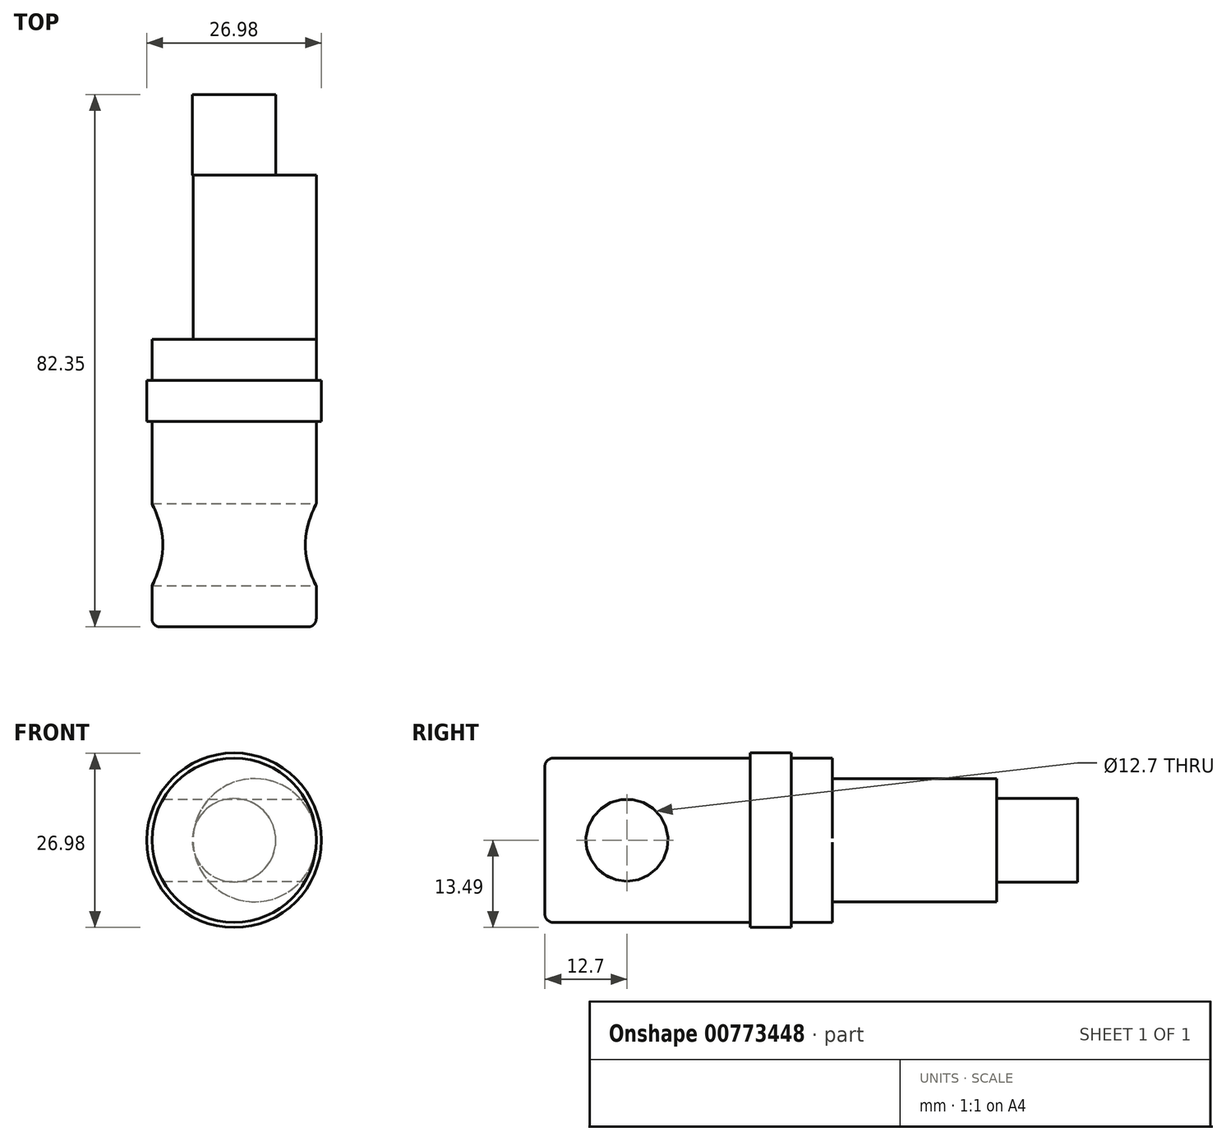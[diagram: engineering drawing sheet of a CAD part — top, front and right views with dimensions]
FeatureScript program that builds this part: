
annotation { "Feature Type Name" : "Feature", "Feature Type Description" : "" }
export const myFeature = defineFeature(function(context is Context, id is Id, definition is map)
    precondition{}
    {
        {
            var Q0;
            Q0=qCreatedBy(makeId("Front.planeOp"),FACE);
            var sketch = newSketch(context, id + "F0", { "sketchPlane" : qUnion([Q0])});
            skCircle(sketch, "E0", {"center": v(0, 0) * mm, "radius": 6.45 * mm});
            skSolve(sketch);
        }
        {
            var Q0;
            Q0 = qSketchRegion(id + "F0", true);
            extrude(context, id + "F1", {"entities" : qUnion([Q0]), "depth" : 12.5 * mm, "offsetDistance" : 25.4 * mm});
        }
        {
            var Q0;
            Q0=makeQuery(id+"F1.opExtrude","CAP_FACE",FACE,{"disambiguationData":[OSD([sQuery(id+"F0.wireOp",EDGE,"E0")])],"isStart":false});
            var sketch = newSketch(context, id + "F2", { "sketchPlane" : qUnion([Q0])});
            skPoint(sketch, "E1", {"position": v(3.18, 0) * mm});
            skCircle(sketch, "E2", {"center": v(3.18, 0) * mm, "radius": 9.52 * mm});
            skSolve(sketch);
        }
        {
            var Q0;
            Q0 = qSketchRegion(id + "F2", true);
            extrude(context, id + "F3", {"entities" : qUnion([Q0]), "operationType" : NewBodyOperationType.ADD, "depth" : 25.4 * mm, "offsetDistance" : 25.4 * mm});
        }
        {
            var Q0;
            Q0=makeQuery(id+"F3.opExtrude","CAP_FACE",FACE,{"disambiguationData":[OSD([sQuery(id+"F2.wireOp",EDGE,"E2")])],"isStart":false});
            var sketch = newSketch(context, id + "F4", { "sketchPlane" : qUnion([Q0])});
            skCircle(sketch, "E3", {"center": v(0, 0) * mm, "radius": 12.7 * mm});
            skSolve(sketch);
        }
        {
            var Q0;
            Q0 = qSketchRegion(id + "F4", true);
            extrude(context, id + "F5", {"entities" : qUnion([Q0]), "operationType" : NewBodyOperationType.ADD, "depth" : 6.35 * mm, "offsetDistance" : 25.4 * mm});
        }
        {
            var Q0;
            Q0=makeQuery(id+"F5.opExtrude","CAP_FACE",FACE,{"disambiguationData":[OSD([sQuery(id+"F4.wireOp",EDGE,"E3")])],"isStart":false});
            var sketch = newSketch(context, id + "F6", { "sketchPlane" : qUnion([Q0])});
            skCircle(sketch, "E4", {"center": v(0, 0) * mm, "radius": 13.5 * mm});
            skSolve(sketch);
        }
        {
            var Q0;
            Q0 = qSketchRegion(id + "F6", true);
            extrude(context, id + "F7", {"entities" : qUnion([Q0]), "operationType" : NewBodyOperationType.ADD, "depth" : 6.35 * mm, "offsetDistance" : 25.4 * mm});
        }
        {
            var Q0;
            Q0=makeQuery(id+"F7.opExtrude","CAP_FACE",FACE,{"disambiguationData":[OSD([sQuery(id+"F6.wireOp",EDGE,"E4")])],"isStart":false});
            var sketch = newSketch(context, id + "F8", { "sketchPlane" : qUnion([Q0])});
            skCircle(sketch, "E5", {"center": v(0, 0) * mm, "radius": 12.7 * mm});
            skSolve(sketch);
        }
        {
            var Q0;
            Q0 = qSketchRegion(id + "F8", true);
            extrude(context, id + "F9", {"entities" : qUnion([Q0]), "operationType" : NewBodyOperationType.ADD, "depth" : 31.75 * mm, "offsetDistance" : 25.4 * mm});
        }
        {
            var Q0;
            Q0=qCreatedBy(makeId("Right.planeOp"),FACE);
            var sketch = newSketch(context, id + "F10", { "sketchPlane" : qUnion([Q0])});
            skPoint(sketch, "E6", {"position": v(-69.65, 0) * mm});
            skCircle(sketch, "E7", {"center": v(-69.65, 0) * mm, "radius": 6.35 * mm});
            skSolve(sketch);
        }
        {
            var Q0;
            Q0 = qSketchRegion(id + "F10", true);
            extrude(context, id + "F11", {"entities" : qUnion([Q0]), "operationType" : NewBodyOperationType.REMOVE, "oppositeDirection" : true, "depth" : 31.9 * mm, "offsetDistance" : 25.4 * mm, "symmetric" : true});
        }
        {
            var Q0;
            Q0=makeQuery(id+"F9.opExtrude","CAP_EDGE",EDGE,{"disambiguationData":[OSD([sQuery(id+"F8.wireOp",EDGE,"E5")])],"isStart":false});
            fillet(context, id + "F12", {"entities" : qUnion([Q0]), "radius" : 1.27 * mm, "tangentPropagation" : true, "allowEdgeOverflow" : false});
        }
    });
